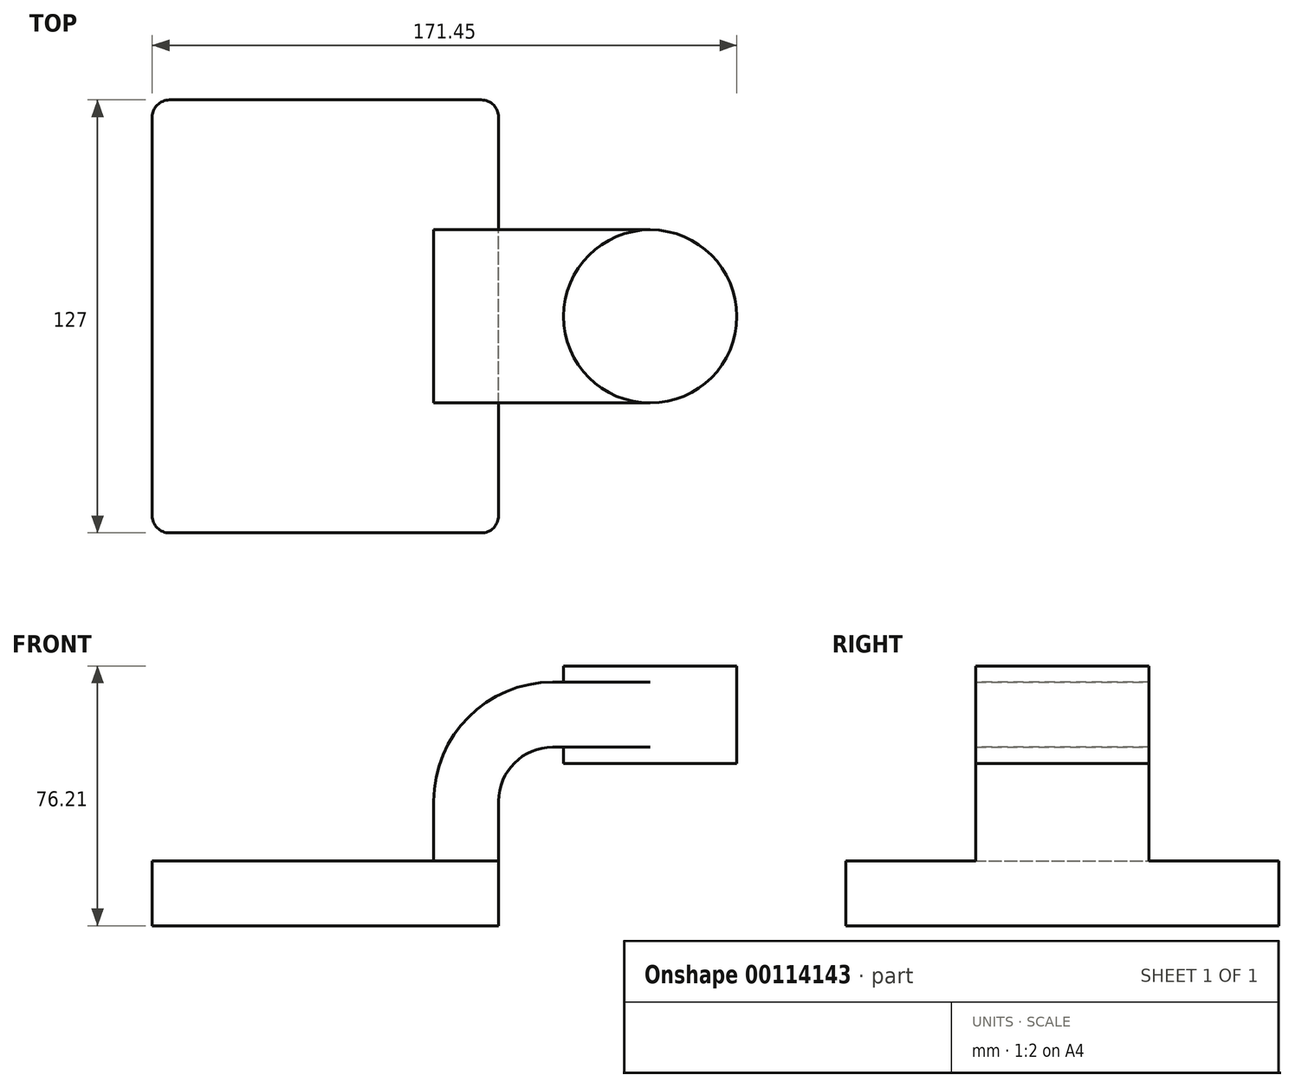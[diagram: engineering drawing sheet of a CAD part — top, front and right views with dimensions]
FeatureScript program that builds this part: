
annotation { "Feature Type Name" : "Feature", "Feature Type Description" : "" }
export const myFeature = defineFeature(function(context is Context, id is Id, definition is map)
    precondition{}
    {
        {
            var Q0;
            Q0=qCreatedBy(makeId("Front.planeOp"),FACE);
            var sketch = newSketch(context, id + "F0", { "sketchPlane" : qUnion([Q0])});
            skLineSegment(sketch, "E0.bottom", {"start": v(50.8, -9.52) * mm, "end": v(-50.8, -9.52) * mm});
            skLineSegment(sketch, "E0.top", {"start": v(50.8, 9.53) * mm, "end": v(-50.8, 9.53) * mm});
            skLineSegment(sketch, "E0.left", {"start": v(50.8, -9.52) * mm, "end": v(50.8, 9.53) * mm});
            skLineSegment(sketch, "E0.right", {"start": v(-50.8, -9.53) * mm, "end": v(-50.8, 9.53) * mm});
            skPoint(sketch, "E0.middle", {"position": v(0, 0) * mm});
            skLineSegment(sketch, "E1.bottom", {"start": v(120.65, 38.1) * mm, "end": v(69.85, 38.1) * mm});
            skLineSegment(sketch, "E1.top", {"start": v(120.65, 66.68) * mm, "end": v(69.85, 66.68) * mm});
            skLineSegment(sketch, "E1.left", {"start": v(120.65, 38.1) * mm, "end": v(120.65, 66.68) * mm});
            skLineSegment(sketch, "E1.right", {"start": v(69.85, 38.1) * mm, "end": v(69.85, 66.68) * mm});
            skPoint(sketch, "E1.middle", {"position": v(95.25, 52.39) * mm});
            skLineSegment(sketch, "E2", {"start": v(50.8, 9.53) * mm, "end": v(50.8, 26.99) * mm});
            skArc(sketch, "E3", {"start": v(50.8, 26.99) * mm, "mid": v(55.45, 38.21) * mm, "end": v(66.67, 42.86) * mm});
            skLineSegment(sketch, "E4", {"start": v(66.67, 42.86) * mm, "end": v(95.25, 42.86) * mm});
            skLineSegment(sketch, "E5.0", {"start": v(66.67, 61.91) * mm, "end": v(95.25, 61.91) * mm});
            skArc(sketch, "E5.1", {"start": v(31.75, 26.99) * mm, "mid": v(41.98, 51.68) * mm, "end": v(66.67, 61.91) * mm});
            skLineSegment(sketch, "E5.2", {"start": v(31.75, 9.53) * mm, "end": v(31.75, 26.99) * mm});
            skPoint(sketch, "E6.startSnap0", {"position": v(95.25, 66.68) * mm});
            skLineSegment(sketch, "E7", {"start": v(95.25, 66.68) * mm, "end": v(95.25, 38.1) * mm});
            skFitSpline(sketch, "E8", {"points": [v(-50.8, 9.53) * mm, v(66.67, 61.91) * mm], "startDerivative": vector(25.82, 74.8) * mm, "endDerivative": vector(196.37, -2.26) * mm});
            skSolve(sketch);
        }
        {
            var Q0;
            Q0=makeQuery(id+"F0.imprint","IMPRINT",FACE,{"disambiguationData":[TD([[makeQuery(id+"F0.imprint","IMPRINT",EDGE,{"derivedFrom":sQuery(id+"F0.wireOp",EDGE,"E0.bottom")}),-1.0]])]});
            extrude(context, id + "F1", {"entities" : qUnion([Q0]), "endBound" : BoundingType.SYMMETRIC, "depth" : 127 * mm});
        }
        {
            var Q0;
            {var subQ1=sQuery(id+"F0.wireOp",EDGE,"E2");Q0=makeQuery(id+"F0.imprint","IMPRINT",FACE,{"disambiguationData":[TD([[makeQuery(id+"F0.imprint","IMPRINT",EDGE,{"derivedFrom":subQ1}),1.0]])]});}
            var Q1;
            {var subQ0=sQuery(id+"F0.wireOp",EDGE,"E4");var subQ1=sQuery(id+"F0.wireOp",EDGE,"E1.right");var subQ2=makeQuery(id+"F0.imprint","INTERSECT",VERTEX,{"derivedFrom":[subQ1,subQ0]});Q1=makeQuery(id+"F0.imprint","IMPRINT",FACE,{"disambiguationData":[TD([[makeQuery(id+"F0.imprint","IMPRINT",EDGE,{"disambiguationData":[TD([[subQ2,-1.0]])],"derivedFrom":subQ1}),-1.0]])]});}
            extrude(context, id + "F2", {"entities" : qUnion([Q0, Q1]), "operationType" : NewBodyOperationType.ADD, "endBound" : BoundingType.SYMMETRIC, "depth" : 50.8 * mm});
        }
        {
            var Q0;
            Q0=makeQuery(id+"F0.imprint","IMPRINT",FACE,{"disambiguationData":[TD([[makeQuery(id+"F0.imprint","IMPRINT",EDGE,{"derivedFrom":sQuery(id+"F0.wireOp",EDGE,"E5.1")}),1.0]])]});
            extrude(context, id + "F3", {"entities" : qUnion([Q0]), "operationType" : NewBodyOperationType.ADD, "endBound" : BoundingType.SYMMETRIC, "depth" : 15.88 * mm});
        }
        {
            var Q0;
            {var subQ0=sQuery(id+"F0.wireOp",EDGE,"E1.left");Q0=makeQuery(id+"F0.imprint","IMPRINT",FACE,{"disambiguationData":[TD([[makeQuery(id+"F0.imprint","IMPRINT",EDGE,{"derivedFrom":subQ0}),1.0]])]});}
            var Q1;
            Q1=sQuery(id+"F0.wireOp",EDGE,"E7");
            revolve(context, id + "F4", {"operationType" : NewBodyOperationType.ADD, "entities" : qUnion([Q0]), "axis" : qUnion([Q1]), "revolveType" : RevolveType.FULL});
        }
        {
            var Q0;
            Q0=makeQuery(id+"F1.opExtrude","CAP_EDGE",EDGE,{"disambiguationData":[OSD([sQuery(id+"F0.wireOp",EDGE,"E0.right")])],"isStart":false});
            var Q1;
            Q1=makeQuery(id+"F1.opExtrude","CAP_EDGE",EDGE,{"disambiguationData":[OSD([sQuery(id+"F0.wireOp",EDGE,"E0.left")])],"isStart":false});
            var Q2;
            Q2=makeQuery(id+"F1.opExtrude","CAP_EDGE",EDGE,{"disambiguationData":[OSD([sQuery(id+"F0.wireOp",EDGE,"E0.left")])],"isStart":true});
            var Q3;
            Q3=makeQuery(id+"F1.opExtrude","CAP_EDGE",EDGE,{"disambiguationData":[OSD([sQuery(id+"F0.wireOp",EDGE,"E0.right")])],"isStart":true});
            fillet(context, id + "F5", {"entities" : qUnion([Q0, Q1, Q2, Q3]), "radius" : 5.08 * mm, "tangentPropagation" : true, "allowEdgeOverflow" : false});
        }
    });
